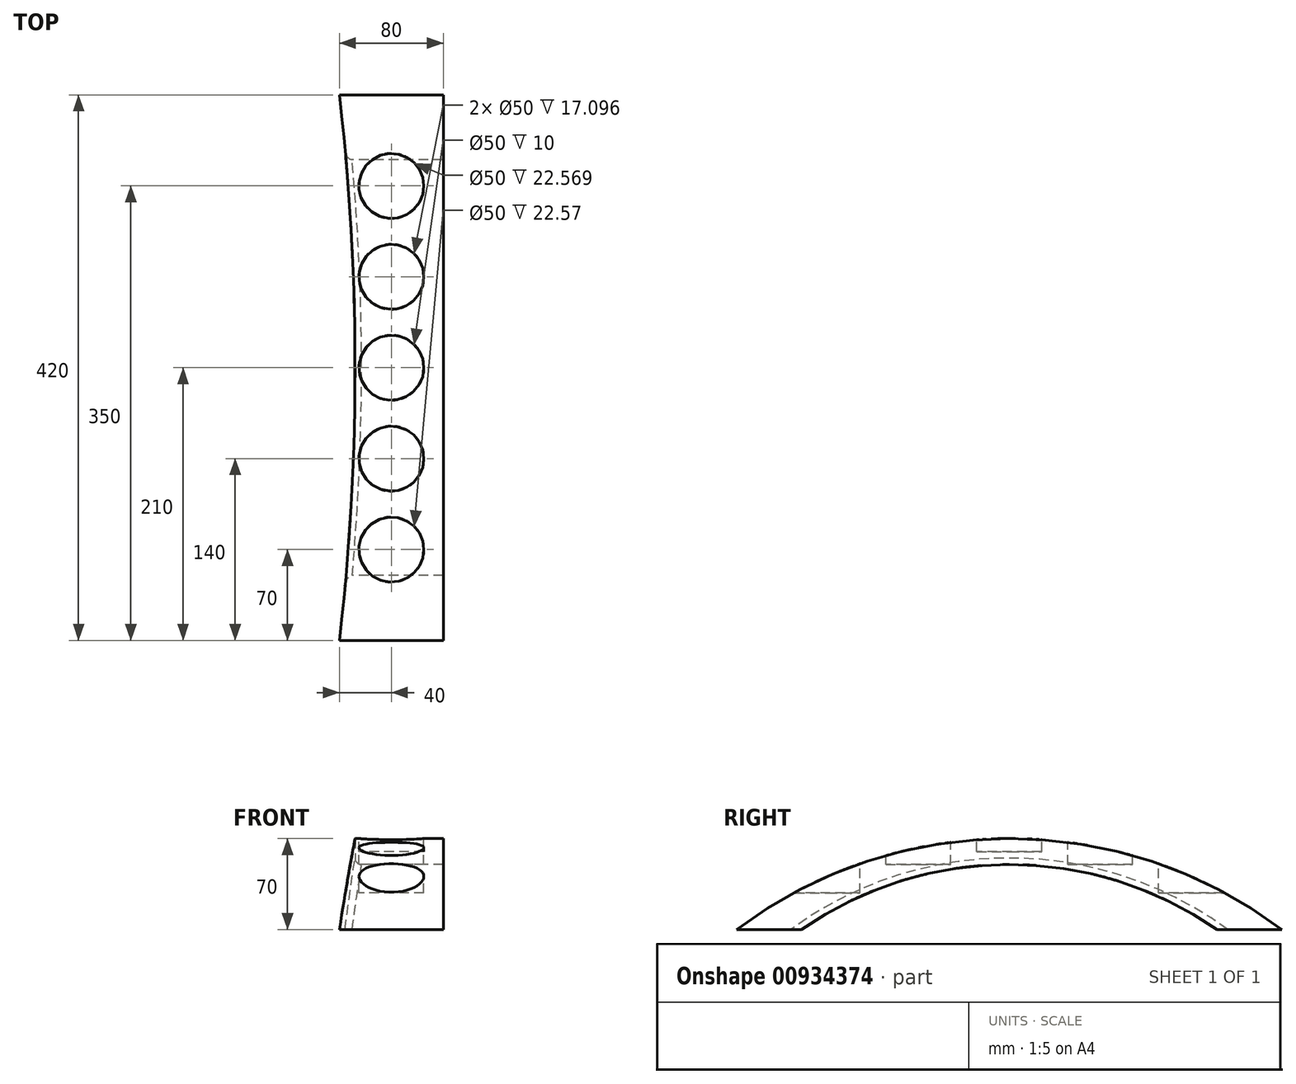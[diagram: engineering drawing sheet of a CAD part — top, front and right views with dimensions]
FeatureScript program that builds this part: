
annotation { "Feature Type Name" : "Feature", "Feature Type Description" : "" }
export const myFeature = defineFeature(function(context is Context, id is Id, definition is map)
    precondition{}
    {
        {
            var Q0;
            Q0=qCreatedBy(makeId("Right.planeOp"),FACE);
            var sketch = newSketch(context, id + "F0", { "sketchPlane" : qUnion([Q0])});
            skArc(sketch, "E0", {"start": v(160, 0) * mm, "mid": v(0, 50) * mm, "end": v(-160, 0) * mm});
            skLineSegment(sketch, "E1", {"start": v(-160, 0) * mm, "end": v(-210, 0) * mm});
            skLineSegment(sketch, "E2", {"start": v(160, 0) * mm, "end": v(210, 0) * mm});
            skArc(sketch, "E3", {"start": v(210, 0) * mm, "mid": v(0, 70) * mm, "end": v(-210, 0) * mm});
            skSolve(sketch);
        }
        {
            var Q0;
            Q0 = qSketchRegion(id + "F0", true);
            extrude(context, id + "F1", {"entities" : qUnion([Q0]), "depth" : 40 * mm, "offsetDistance" : 25 * mm, "hasSecondDirection" : true, "secondDirectionOppositeDirection" : true, "secondDirectionDepth" : 40 * mm});
        }
        {
            var Q0;
            Q0=qCreatedBy(makeId("Top.planeOp"),FACE);
            var sketch = newSketch(context, id + "F2", { "sketchPlane" : qUnion([Q0])});
            skArc(sketch, "E4", {"start": v(-40, -210) * mm, "mid": v(-28, 0) * mm, "end": v(-40, 210) * mm});
            skLineSegment(sketch, "E5.0", {"start": v(-40, 210) * mm, "end": v(-40, -210) * mm});
            skSolve(sketch);
        }
        {
            var Q0;
            Q0 = qSketchRegion(id + "F2", true);
            extrude(context, id + "F3", {"entities" : qUnion([Q0]), "operationType" : NewBodyOperationType.REMOVE, "endBound" : BoundingType.THROUGH_ALL, "depth" : 25 * mm, "offsetDistance" : 25 * mm});
        }
        {
            var Q0;
            Q0=qCreatedBy(makeId("Top.planeOp"),FACE);
            cPlane(context, id + "F4", {"entities" : qUnion([Q0]), "cplaneType" : CPlaneType.OFFSET, "offset" : 80 * mm, "width" : 150 * mm, "height" : 150 * mm});
        }
        {
            var Q0;
            Q0=qCreatedBy(id+"F4.planeOp",FACE);
            var sketch = newSketch(context, id + "F5", { "sketchPlane" : qUnion([Q0])});
            skCircle(sketch, "E6", {"center": v(0, 0) * mm, "radius": 25 * mm});
            skCircle(sketch, "E7", {"center": v(0, 70) * mm, "radius": 25 * mm});
            skCircle(sketch, "E8", {"center": v(0, 140) * mm, "radius": 25 * mm});
            skCircle(sketch, "E9", {"center": v(0, -70) * mm, "radius": 25 * mm});
            skCircle(sketch, "E10", {"center": v(0, -140) * mm, "radius": 25 * mm});
            skSolve(sketch);
        }
        {
            var Q0;
            Q0=qCreatedBy(id+"F4.planeOp",FACE);
            var sketch = newSketch(context, id + "F6", { "sketchPlane" : qUnion([Q0])});
            skCircle(sketch, "E11.0", {"center": v(0, 0) * mm, "radius": 25 * mm});
            skSolve(sketch);
        }
        {
            var Q0;
            Q0 = qSketchRegion(id + "F6", true);
            extrude(context, id + "F7", {"entities" : qUnion([Q0]), "operationType" : NewBodyOperationType.REMOVE, "oppositeDirection" : true, "depth" : 20 * mm, "offsetDistance" : 25 * mm});
        }
        {
            var Q0;
            Q0=qCreatedBy(id+"F4.planeOp",FACE);
            var sketch = newSketch(context, id + "F8", { "sketchPlane" : qUnion([Q0])});
            skCircle(sketch, "E12.0", {"center": v(0, -70) * mm, "radius": 25 * mm});
            skCircle(sketch, "E13.0", {"center": v(0, 70) * mm, "radius": 25 * mm});
            skSolve(sketch);
        }
        {
            var Q0;
            Q0 = qSketchRegion(id + "F8", true);
            extrude(context, id + "F9", {"entities" : qUnion([Q0]), "operationType" : NewBodyOperationType.REMOVE, "oppositeDirection" : true, "depth" : 30 * mm, "offsetDistance" : 25 * mm});
        }
        {
            var Q0;
            Q0=qCreatedBy(id+"F4.planeOp",FACE);
            var sketch = newSketch(context, id + "F10", { "sketchPlane" : qUnion([Q0])});
            skCircle(sketch, "E14.0", {"center": v(0, -140) * mm, "radius": 25 * mm});
            skCircle(sketch, "E15.0", {"center": v(0, 140) * mm, "radius": 25 * mm});
            skSolve(sketch);
        }
        {
            var Q0;
            Q0 = qSketchRegion(id + "F10", true);
            extrude(context, id + "F11", {"entities" : qUnion([Q0]), "operationType" : NewBodyOperationType.REMOVE, "oppositeDirection" : true, "depth" : 52 * mm, "offsetDistance" : 25 * mm});
        }
        {
            var Q0;
            Q0=makeQuery(id+"F07JK4nRUnn33jq_1.1.F3.boolean.opBoolean","INTERSECT",EDGE,{"derivedFrom":[makeQuery(id+"F1.opExtrude","SWEPT_FACE",FACE,{"disambiguationData":[OSD([sQuery(id+"F0.wireOp",EDGE,"E0")])]}),makeQuery(id+"F07JK4nRUnn33jq_1.1.F3.opExtrude","SWEPT_FACE",FACE,{"disambiguationData":[OSD([sQuery(id+"F2.wireOp",EDGE,"E4")])]})]});
            var Q1;
            Q1=makeQuery(id+"F3.boolean.opBoolean","INTERSECT",EDGE,{"derivedFrom":[makeQuery(id+"F1.opExtrude","SWEPT_FACE",FACE,{"disambiguationData":[OSD([sQuery(id+"F0.wireOp",EDGE,"E0")])]}),makeQuery(id+"F3.opExtrude","SWEPT_FACE",FACE,{"disambiguationData":[OSD([sQuery(id+"F2.wireOp",EDGE,"E4")])]})]});
            fillet(context, id + "F12", {"entities" : qUnion([Q0, Q1]), "radius" : 5 * mm, "tangentPropagation" : true, "allowEdgeOverflow" : false});
        }
    });
